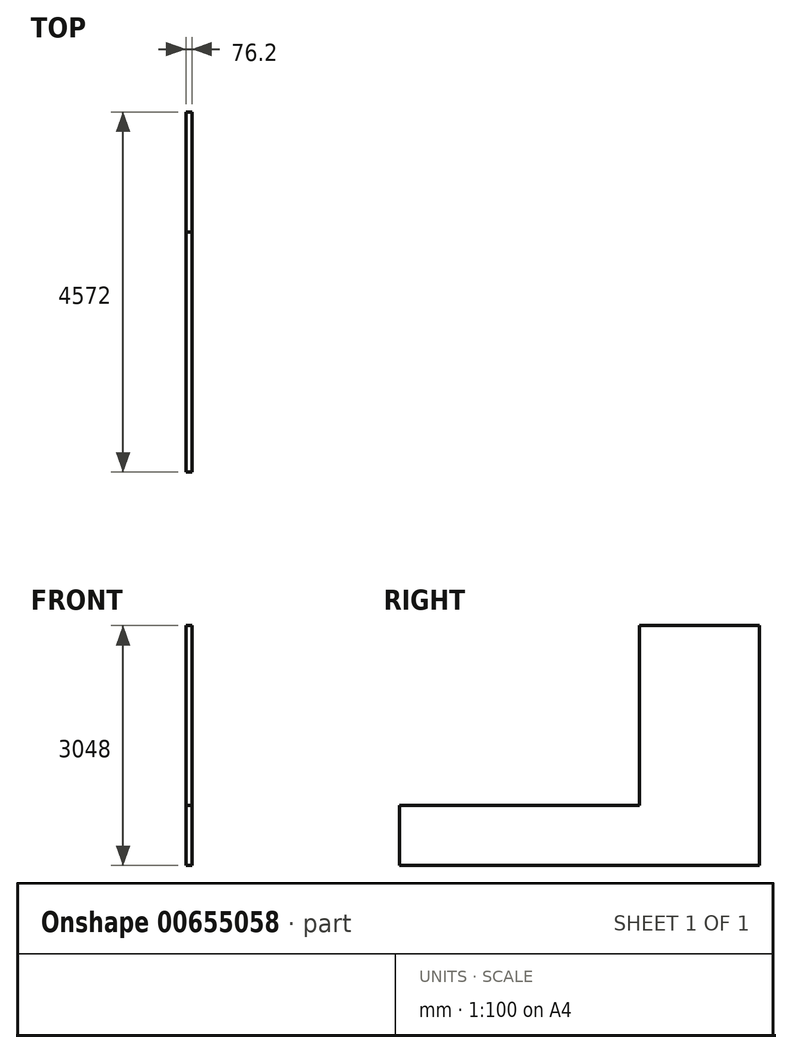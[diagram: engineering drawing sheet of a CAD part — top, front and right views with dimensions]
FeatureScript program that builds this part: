
annotation { "Feature Type Name" : "Feature", "Feature Type Description" : "" }
export const myFeature = defineFeature(function(context is Context, id is Id, definition is map)
    precondition{}
    {
        {
            var Q0;
            Q0=qCreatedBy(makeId("Top.planeOp"),FACE);
            var sketch = newSketch(context, id + "F0", { "sketchPlane" : qUnion([Q0])});
            skLineSegment(sketch, "E0.bottom", {"start": v(0, 0) * mm, "end": v(-76.2, 0) * mm});
            skLineSegment(sketch, "E0.top", {"start": v(0, -4572) * mm, "end": v(-76.2, -4572) * mm});
            skLineSegment(sketch, "E0.left", {"start": v(0, 0) * mm, "end": v(0, -4572) * mm});
            skLineSegment(sketch, "E0.right", {"start": v(-76.2, 0) * mm, "end": v(-76.2, -4572) * mm});
            skSolve(sketch);
        }
        {
            var Q0;
            Q0=makeQuery(id+"F0.imprint","IMPRINT",FACE,{"disambiguationData":[TD([[makeQuery(id+"F0.imprint","IMPRINT",EDGE,{"derivedFrom":sQuery(id+"F0.wireOp",EDGE,"E0.bottom")}),1.0]])]});
            extrude(context, id + "F1", {"entities" : qUnion([Q0]), "depth" : 3048 * mm, "offsetDistance" : 25.4 * mm});
        }
        {
            var Q0;
            Q0=makeQuery(id+"F1.opExtrude","SWEPT_FACE",FACE,{"disambiguationData":[OSD([sQuery(id+"F0.wireOp",EDGE,"E0.right")])]});
            var sketch = newSketch(context, id + "F2", { "sketchPlane" : qUnion([Q0])});
            skLineSegment(sketch, "E1.bottom", {"start": v(4572, 3048) * mm, "end": v(1524, 3048) * mm});
            skLineSegment(sketch, "E1.top", {"start": v(4572, 762) * mm, "end": v(1524, 762) * mm});
            skLineSegment(sketch, "E1.left", {"start": v(4572, 3048) * mm, "end": v(4572, 762) * mm});
            skLineSegment(sketch, "E1.right", {"start": v(1524, 3048) * mm, "end": v(1524, 762) * mm});
            skSolve(sketch);
        }
        {
            var Q0;
            Q0=makeQuery(id+"F2.imprint","IMPRINT",FACE,{"disambiguationData":[TD([[makeQuery(id+"F2.imprint","IMPRINT",EDGE,{"derivedFrom":sQuery(id+"F2.wireOp",EDGE,"E1.bottom")}),-1.0]])]});
            extrude(context, id + "F3", {"entities" : qUnion([Q0]), "operationType" : NewBodyOperationType.REMOVE, "endBound" : BoundingType.UP_TO_NEXT, "oppositeDirection" : true, "depth" : 25.4 * mm, "offsetDistance" : 25.4 * mm});
        }
    });
